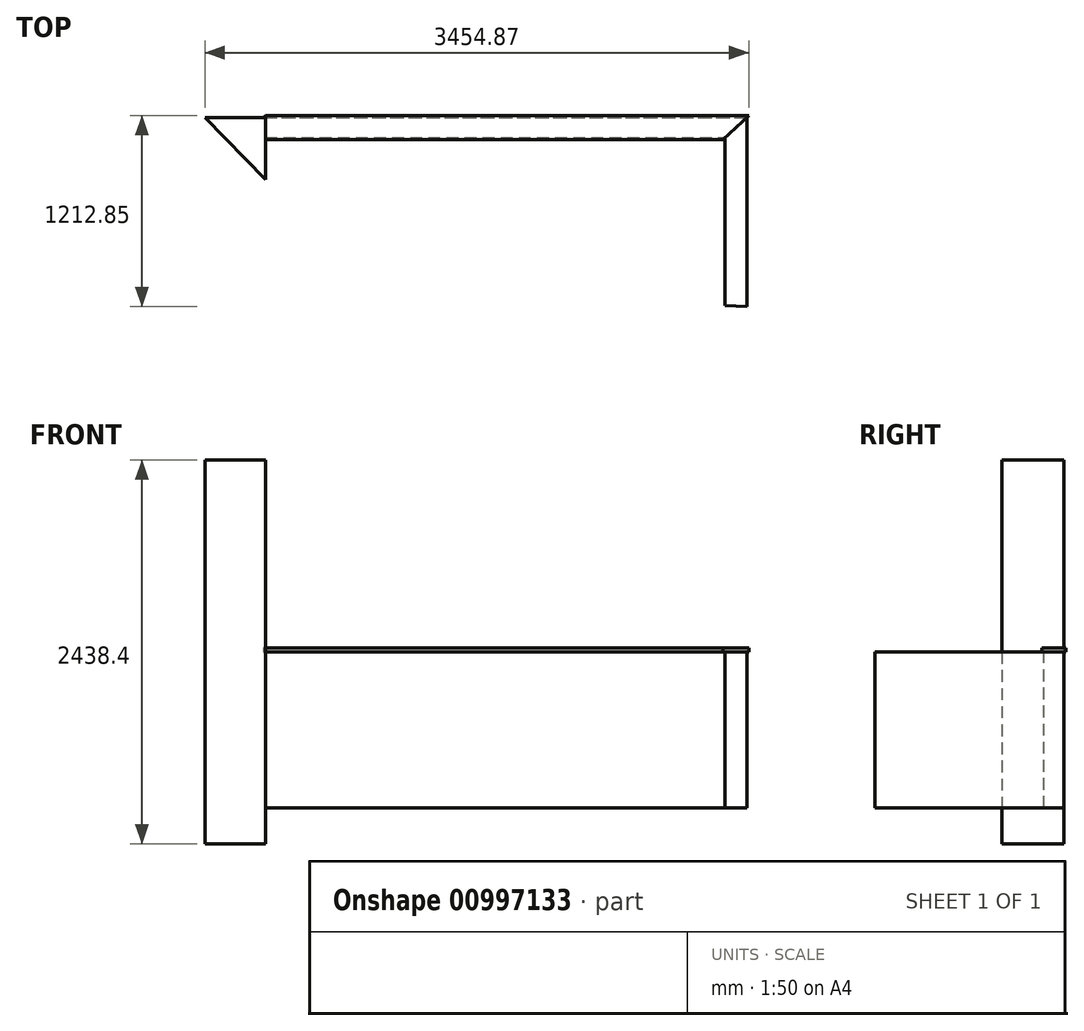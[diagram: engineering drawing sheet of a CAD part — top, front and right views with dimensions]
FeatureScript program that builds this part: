
annotation { "Feature Type Name" : "Feature", "Feature Type Description" : "" }
export const myFeature = defineFeature(function(context is Context, id is Id, definition is map)
    precondition{}
    {
        {
            var Q0;
            Q0=qCreatedBy(makeId("Top.planeOp"),FACE);
            var sketch = newSketch(context, id + "F0", { "sketchPlane" : qUnion([Q0])});
            skLineSegment(sketch, "E0", {"start": v(-849.39, 0) * mm, "end": v(-464.74, 0) * mm});
            skLineSegment(sketch, "E1", {"start": v(-464.74, 0) * mm, "end": v(-464.74, -393.56) * mm});
            skLineSegment(sketch, "E2.bottom", {"start": v(-464.74, 0) * mm, "end": v(2592.78, 0) * mm});
            skLineSegment(sketch, "E2.top", {"start": v(-464.74, -127) * mm, "end": v(2453.08, -127) * mm});
            skLineSegment(sketch, "E2.left", {"start": v(-464.74, 0) * mm, "end": v(-464.74, -127) * mm});
            skLineSegment(sketch, "E3.left", {"start": v(2592.78, 0) * mm, "end": v(2592.78, -1200.15) * mm});
            skLineSegment(sketch, "E3.right", {"start": v(2453.08, -127) * mm, "end": v(2453.08, -1193.8) * mm});
            skLineSegment(sketch, "E4", {"start": v(-849.39, 0) * mm, "end": v(-464.74, -393.56) * mm});
            skLineSegment(sketch, "E5", {"start": v(2453.08, -1193.8) * mm, "end": v(2592.78, -1200.15) * mm});
            skSolve(sketch);
        }
        {
            var Q0;
            {var subQ2=sQuery(id+"F0.wireOp",EDGE,"E2.top");Q0=makeQuery(id+"F0.imprint","IMPRINT",FACE,{"disambiguationData":[TD([[makeQuery(id+"F0.imprint","IMPRINT",EDGE,{"derivedFrom":subQ2}),1.0]])]});}
            extrude(context, id + "F1", {"entities" : qUnion([Q0]), "oppositeDirection" : true, "depth" : 990.6 * mm, "offsetDistance" : 25.4 * mm});
        }
        {
            var Q0;
            Q0=makeQuery(id+"F0.imprint","IMPRINT",FACE,{"disambiguationData":[TD([[makeQuery(id+"F0.imprint","IMPRINT",EDGE,{"derivedFrom":sQuery(id+"F0.wireOp",EDGE,"E0")}),-1.0]])]});
            extrude(context, id + "F2", {"entities" : qUnion([Q0]), "operationType" : NewBodyOperationType.ADD, "endBound" : BoundingType.SYMMETRIC, "depth" : 2438.4 * mm, "offsetDistance" : 25.4 * mm});
        }
        {
            var Q0;
            Q0=makeQuery(id+"F0.imprint","IMPRINT",FACE,{"disambiguationData":[TD([[makeQuery(id+"F0.imprint","IMPRINT",EDGE,{"derivedFrom":sQuery(id+"F0.wireOp",EDGE,"E2.bottom")}),-1.0]])]});
            var sketch = newSketch(context, id + "F3", { "sketchPlane" : qUnion([Q0])});
            skLineSegment(sketch, "E6.0", {"start": v(-464.77, -139.7) * mm, "end": v(2440.38, -139.7) * mm});
            skLineSegment(sketch, "E7.0", {"start": v(2440.38, -139.7) * mm, "end": v(2440.38, -1205.94) * mm});
            skLineSegment(sketch, "E8.0", {"start": v(2605.48, 12.7) * mm, "end": v(2605.48, -1212.85) * mm});
            skLineSegment(sketch, "E9.0", {"start": v(-464.77, 12.7) * mm, "end": v(2605.48, 12.7) * mm});
            skLineSegment(sketch, "E10", {"start": v(-464.77, 0) * mm, "end": v(-464.77, -139.7) * mm});
            skPoint(sketch, "E11.orphan", {"position": v(-467.23, -139.7) * mm});
            skLineSegment(sketch, "E12", {"start": v(-464.77, 12.7) * mm, "end": v(-477.47, 0) * mm});
            skLineSegment(sketch, "E13", {"start": v(-464.77, 0) * mm, "end": v(-477.47, 0) * mm});
            skLineSegment(sketch, "E14", {"start": v(2440.38, -139.7) * mm, "end": v(2605.48, 12.7) * mm});
            skLineSegment(sketch, "E15.0", {"start": v(2440.38, -1205.94) * mm, "end": v(2605.48, -1213.44) * mm});
            skSolve(sketch);
        }
        {
            var Q0;
            Q0 = qSketchRegion(id + "F3", true);
            extrude(context, id + "F4", {"entities" : qUnion([Q0]), "operationType" : NewBodyOperationType.ADD, "depth" : 25.4 * mm, "offsetDistance" : 25.4 * mm});
        }
    });
